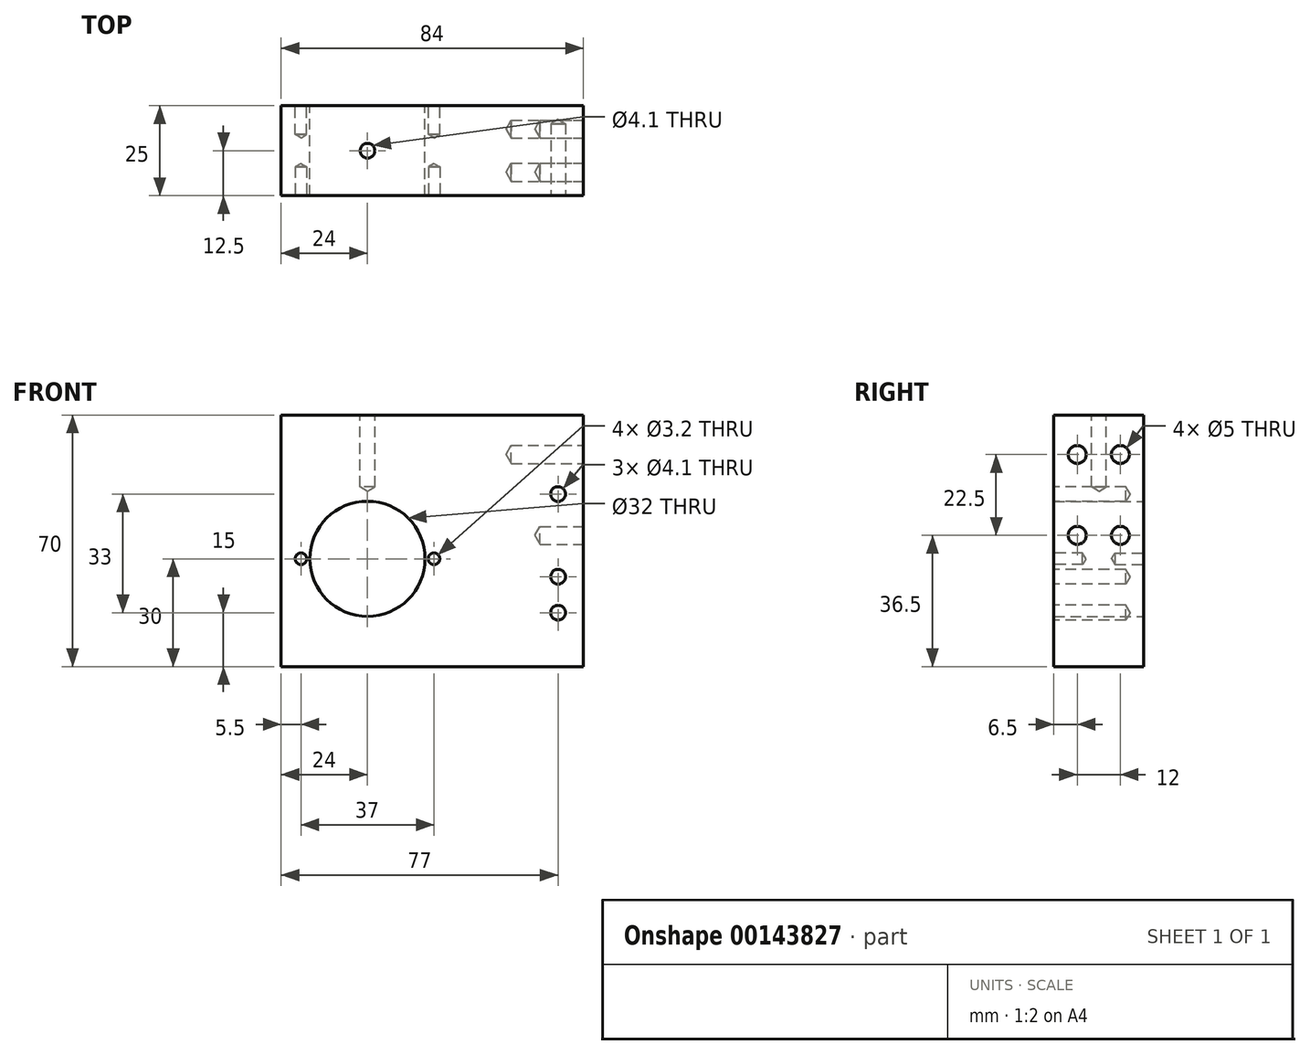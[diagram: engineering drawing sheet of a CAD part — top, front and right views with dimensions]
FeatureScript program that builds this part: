
annotation { "Feature Type Name" : "Feature", "Feature Type Description" : "" }
export const myFeature = defineFeature(function(context is Context, id is Id, definition is map)
    precondition{}
    {
        {
            var Q0;
            Q0=qCreatedBy(makeId("Front.planeOp"),FACE);
            var sketch = newSketch(context, id + "F0", { "sketchPlane" : qUnion([Q0])});
            skLineSegment(sketch, "E0.bottom", {"start": v(42, -35) * mm, "end": v(-42, -35) * mm});
            skLineSegment(sketch, "E0.top", {"start": v(42, 35) * mm, "end": v(-42, 35) * mm});
            skLineSegment(sketch, "E0.left", {"start": v(42, -35) * mm, "end": v(42, 35) * mm});
            skLineSegment(sketch, "E0.right", {"start": v(-42, -35) * mm, "end": v(-42, 35) * mm});
            skPoint(sketch, "E0.middle", {"position": v(0, 0) * mm});
            skCircle(sketch, "E1", {"center": v(-18, -5) * mm, "radius": 16 * mm});
            skSolve(sketch);
        }
        {
            var Q0;
            Q0=makeQuery(id+"F0.imprint","IMPRINT",FACE,{"disambiguationData":[TD([[makeQuery(id+"F0.imprint","IMPRINT",EDGE,{"derivedFrom":sQuery(id+"F0.wireOp",EDGE,"E0.bottom")}),-1.0]])]});
            extrude(context, id + "F1", {"entities" : qUnion([Q0]), "depth" : 25 * mm});
        }
        {
            var Q0;
            Q0=makeQuery(id+"F1.opExtrude","CAP_FACE",FACE,{"disambiguationData":[OSD([sQuery(id+"F0.wireOp",EDGE,"E0.bottom"),sQuery(id+"F0.wireOp",EDGE,"E0.top"),sQuery(id+"F0.wireOp",EDGE,"E0.left"),sQuery(id+"F0.wireOp",EDGE,"E0.right"),sQuery(id+"F0.wireOp",EDGE,"E1")])],"isStart":false});
            var sketch = newSketch(context, id + "F2", { "sketchPlane" : qUnion([Q0])});
            skCircle(sketch, "E2", {"center": v(-36.5, -5) * mm, "radius": 1.85 * mm});
            skCircle(sketch, "E3", {"center": v(0.5, -5) * mm, "radius": 1.8 * mm});
            skSolve(sketch);
        }
        {
            var Q0;
            Q0=sQuery(id+"F2.wireOp",VERTEX,"E2.center");
            var Q1;
            Q1=sQuery(id+"F2.wireOp",VERTEX,"E3.center");
            var Q2;
            Q2=makeQuery(id+"F1.opExtrude","SWEPT_BODY",BODY,{"disambiguationData":[OSD([sQuery(id+"F0.wireOp",EDGE,"E0.bottom"),sQuery(id+"F0.wireOp",EDGE,"E0.top"),sQuery(id+"F0.wireOp",EDGE,"E0.left"),sQuery(id+"F0.wireOp",EDGE,"E0.right"),sQuery(id+"F0.wireOp",EDGE,"E1")])]});
            hole(context, id + "F3", {"style" : HoleStyle.SIMPLE, "endStyle" : HoleEndStyle.BLIND, "standardTappedOrClearance" : lookupTablePath({ "standard" : "ISO", "engagement" : "75%", "pitch" : "0.75 mm", "size" : "M4", "type" : "Tapped" }), "standardBlindInLast" : lookupTablePath({ "standard" : "ISO", "engagement" : "75%", "pitch" : "0.75 mm", "size" : "M4", "type" : "Tapped" }), "holeDiameter" : 3.2 * mm, "holeDepth" : 8 * mm, "startFromSketch" : true, "locations" : qUnion([Q0, Q1]), "scope" : qUnion([Q2])});
        }
        {
            var Q0;
            Q0=makeQuery(id+"F1.opExtrude","CAP_FACE",FACE,{"disambiguationData":[OSD([sQuery(id+"F0.wireOp",EDGE,"E0.bottom"),sQuery(id+"F0.wireOp",EDGE,"E0.top"),sQuery(id+"F0.wireOp",EDGE,"E0.left"),sQuery(id+"F0.wireOp",EDGE,"E0.right"),sQuery(id+"F0.wireOp",EDGE,"E1")])],"isStart":false});
            var sketch = newSketch(context, id + "F4", { "sketchPlane" : qUnion([Q0])});
            skCircle(sketch, "E4", {"center": v(35, -10) * mm, "radius": 1.46 * mm});
            skCircle(sketch, "E5", {"center": v(35, -20) * mm, "radius": 1.96 * mm});
            skCircle(sketch, "E6", {"center": v(35, 13) * mm, "radius": 1.62 * mm});
            skSolve(sketch);
        }
        {
            var Q0;
            Q0=sQuery(id+"F4.wireOp",VERTEX,"E6.center");
            var Q1;
            Q1=sQuery(id+"F4.wireOp",VERTEX,"E4.center");
            var Q2;
            Q2=sQuery(id+"F4.wireOp",VERTEX,"E5.center");
            var Q3;
            Q3=makeQuery(id+"F1.opExtrude","SWEPT_BODY",BODY,{"disambiguationData":[OSD([sQuery(id+"F0.wireOp",EDGE,"E0.bottom"),sQuery(id+"F0.wireOp",EDGE,"E0.top"),sQuery(id+"F0.wireOp",EDGE,"E0.left"),sQuery(id+"F0.wireOp",EDGE,"E0.right"),sQuery(id+"F0.wireOp",EDGE,"E1")])]});
            hole(context, id + "F5", {"style" : HoleStyle.SIMPLE, "endStyle" : HoleEndStyle.BLIND, "standardTappedOrClearance" : lookupTablePath({ "standard" : "ISO", "engagement" : "75%", "pitch" : "0.9 mm", "size" : "M5", "type" : "Tapped" }), "standardBlindInLast" : lookupTablePath({ "standard" : "ISO", "engagement" : "75%", "pitch" : "0.9 mm", "size" : "M5", "type" : "Tapped" }), "holeDiameter" : 4.1 * mm, "holeDepth" : 20 * mm, "startFromSketch" : true, "locations" : qUnion([Q0, Q1, Q2]), "scope" : qUnion([Q3])});
        }
        {
            var Q0;
            Q0=makeQuery(id+"F1.opExtrude","SWEPT_FACE",FACE,{"disambiguationData":[OSD([sQuery(id+"F0.wireOp",EDGE,"E0.top")])]});
            var sketch = newSketch(context, id + "F6", { "sketchPlane" : qUnion([Q0])});
            skCircle(sketch, "E7", {"center": v(-18, -12.5) * mm, "radius": 2.06 * mm});
            skSolve(sketch);
        }
        {
            var Q0;
            Q0=sQuery(id+"F6.wireOp",VERTEX,"E7.center");
            var Q1;
            Q1=makeQuery(id+"F1.opExtrude","SWEPT_BODY",BODY,{"disambiguationData":[OSD([sQuery(id+"F0.wireOp",EDGE,"E0.bottom"),sQuery(id+"F0.wireOp",EDGE,"E0.top"),sQuery(id+"F0.wireOp",EDGE,"E0.left"),sQuery(id+"F0.wireOp",EDGE,"E0.right"),sQuery(id+"F0.wireOp",EDGE,"E1")])]});
            hole(context, id + "F7", {"style" : HoleStyle.SIMPLE, "endStyle" : HoleEndStyle.BLIND, "standardTappedOrClearance" : lookupTablePath({ "standard" : "ISO", "engagement" : "75%", "pitch" : "0.9 mm", "size" : "M5", "type" : "Tapped" }), "standardBlindInLast" : lookupTablePath({ "standard" : "ISO", "engagement" : "75%", "pitch" : "0.9 mm", "size" : "M5", "type" : "Tapped" }), "holeDiameter" : 4.1 * mm, "holeDepth" : 20 * mm, "startFromSketch" : true, "locations" : qUnion([Q0]), "scope" : qUnion([Q1])});
        }
        {
            var Q0;
            Q0=makeQuery(id+"F1.opExtrude","SWEPT_FACE",FACE,{"disambiguationData":[OSD([sQuery(id+"F0.wireOp",EDGE,"E0.left")])]});
            var sketch = newSketch(context, id + "F8", { "sketchPlane" : qUnion([Q0])});
            skCircle(sketch, "E8", {"center": v(-18.5, 24) * mm, "radius": 1.44 * mm});
            skCircle(sketch, "E9", {"center": v(-6.5, 24) * mm, "radius": 1.33 * mm});
            skSolve(sketch);
        }
        {
            var Q0;
            Q0=sQuery(id+"F8.wireOp",VERTEX,"E8.center");
            var Q1;
            Q1=sQuery(id+"F8.wireOp",VERTEX,"E9.center");
            var Q2;
            Q2=makeQuery(id+"F1.opExtrude","SWEPT_BODY",BODY,{"disambiguationData":[OSD([sQuery(id+"F0.wireOp",EDGE,"E0.bottom"),sQuery(id+"F0.wireOp",EDGE,"E0.top"),sQuery(id+"F0.wireOp",EDGE,"E0.left"),sQuery(id+"F0.wireOp",EDGE,"E0.right"),sQuery(id+"F0.wireOp",EDGE,"E1")])]});
            hole(context, id + "F9", {"style" : HoleStyle.SIMPLE, "endStyle" : HoleEndStyle.BLIND, "standardTappedOrClearance" : lookupTablePath({ "standard" : "ISO", "engagement" : "75%", "pitch" : "1 mm", "size" : "M6", "type" : "Tapped" }), "standardBlindInLast" : lookupTablePath({ "standard" : "ISO", "engagement" : "75%", "pitch" : "1 mm", "size" : "M6", "type" : "Tapped" }), "holeDiameter" : 5 * mm, "holeDepth" : 20 * mm, "startFromSketch" : true, "locations" : qUnion([Q0, Q1]), "scope" : qUnion([Q2]), "majorDiameter" : 6 * mm});
        }
        {
            var Q0;
            Q0=makeQuery(id+"F1.opExtrude","SWEPT_FACE",FACE,{"disambiguationData":[OSD([sQuery(id+"F0.wireOp",EDGE,"E0.left")])]});
            var sketch = newSketch(context, id + "F10", { "sketchPlane" : qUnion([Q0])});
            skCircle(sketch, "E10", {"center": v(-18.5, 1.5) * mm, "radius": 2.44 * mm});
            skCircle(sketch, "E11", {"center": v(-6.5, 1.5) * mm, "radius": 2.58 * mm});
            skSolve(sketch);
        }
        {
            var Q0;
            Q0=sQuery(id+"F10.wireOp",VERTEX,"E10.center");
            var Q1;
            Q1=sQuery(id+"F10.wireOp",VERTEX,"E11.center");
            var Q2;
            Q2=makeQuery(id+"F1.opExtrude","SWEPT_BODY",BODY,{"disambiguationData":[OSD([sQuery(id+"F0.wireOp",EDGE,"E0.bottom"),sQuery(id+"F0.wireOp",EDGE,"E0.top"),sQuery(id+"F0.wireOp",EDGE,"E0.left"),sQuery(id+"F0.wireOp",EDGE,"E0.right"),sQuery(id+"F0.wireOp",EDGE,"E1")])]});
            hole(context, id + "F11", {"style" : HoleStyle.SIMPLE, "endStyle" : HoleEndStyle.BLIND, "holeDiameter" : 5 * mm, "holeDepth" : 12 * mm, "startFromSketch" : true, "locations" : qUnion([Q0, Q1]), "scope" : qUnion([Q2])});
        }
        {
            var Q0;
            Q0=makeQuery(id+"F1.opExtrude","CAP_FACE",FACE,{"disambiguationData":[OSD([sQuery(id+"F0.wireOp",EDGE,"E0.bottom"),sQuery(id+"F0.wireOp",EDGE,"E0.top"),sQuery(id+"F0.wireOp",EDGE,"E0.left"),sQuery(id+"F0.wireOp",EDGE,"E0.right"),sQuery(id+"F0.wireOp",EDGE,"E1")])],"isStart":true});
            var sketch = newSketch(context, id + "F12", { "sketchPlane" : qUnion([Q0])});
            skCircle(sketch, "E12", {"center": v(-0.5, -5) * mm, "radius": 1.28 * mm});
            skCircle(sketch, "E13", {"center": v(36.5, -5) * mm, "radius": 1.65 * mm});
            skSolve(sketch);
        }
        {
            var Q0;
            Q0=sQuery(id+"F12.wireOp",VERTEX,"E12.center");
            var Q1;
            Q1=sQuery(id+"F12.wireOp",VERTEX,"E13.center");
            var Q2;
            Q2=makeQuery(id+"F1.opExtrude","SWEPT_BODY",BODY,{"disambiguationData":[OSD([sQuery(id+"F0.wireOp",EDGE,"E0.bottom"),sQuery(id+"F0.wireOp",EDGE,"E0.top"),sQuery(id+"F0.wireOp",EDGE,"E0.left"),sQuery(id+"F0.wireOp",EDGE,"E0.right"),sQuery(id+"F0.wireOp",EDGE,"E1")])]});
            hole(context, id + "F13", {"style" : HoleStyle.SIMPLE, "endStyle" : HoleEndStyle.BLIND, "standardTappedOrClearance" : lookupTablePath({ "standard" : "ISO", "engagement" : "75%", "pitch" : "0.75 mm", "size" : "M4", "type" : "Tapped" }), "standardBlindInLast" : lookupTablePath({ "standard" : "ISO", "engagement" : "75%", "pitch" : "0.75 mm", "size" : "M4", "type" : "Tapped" }), "holeDiameter" : 3.2 * mm, "holeDepth" : 8 * mm, "startFromSketch" : true, "locations" : qUnion([Q0, Q1]), "scope" : qUnion([Q2])});
        }
    });
